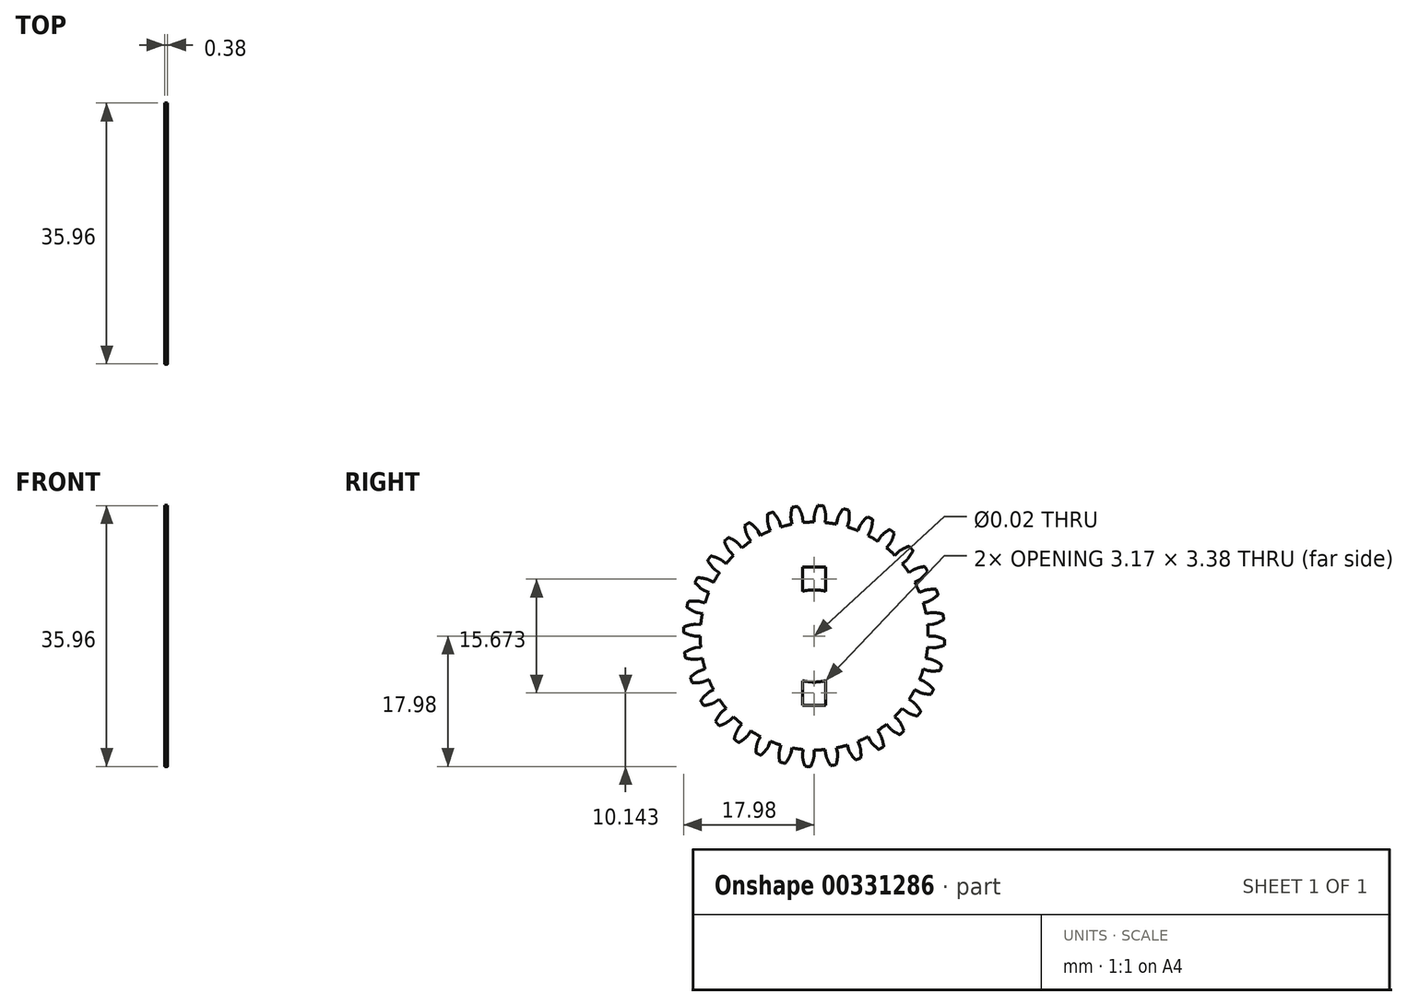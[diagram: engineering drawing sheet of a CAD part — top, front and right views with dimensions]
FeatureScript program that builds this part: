
annotation { "Feature Type Name" : "Feature", "Feature Type Description" : "" }
export const myFeature = defineFeature(function(context is Context, id is Id, definition is map)
    precondition{}
    {
        {
            assignVariable(context, id + "F0", {"name" : "NumberTeeth", "anyValue" : 32});
        }
        {
            assignVariable(context, id + "F1", {"name" : "GearThickness", "anyValue" : 0.38});
        }
        {
            var Q0;
            Q0=qCreatedBy(makeId("Right.planeOp"),FACE);
            var sketch = newSketch(context, id + "F2", { "sketchPlane" : qUnion([Q0])});
            skCircle(sketch, "E0", {"center": v(0, 0) * mm, "radius": 15.7 * mm});
            skCircle(sketch, "E1", {"center": v(0, 0) * mm, "radius": 16.4 * mm, "construction": true});
            skCircle(sketch, "E2", {"center": v(0, 0) * mm, "radius": 16.93 * mm, "construction": true});
            skCircle(sketch, "E3", {"center": v(0, 0) * mm, "radius": 18 * mm});
            skLineSegment(sketch, "E4", {"start": v(0, 0) * mm, "end": v(-16.4, 0) * mm, "construction": true});
            skLineSegment(sketch, "E5.1.0", {"start": v(0, 0) * mm, "end": v(-16.37, 0.82) * mm, "construction": true});
            skLineSegment(sketch, "E5.2.0", {"start": v(0, 0) * mm, "end": v(-16.31, 1.64) * mm, "construction": true});
            skLineSegment(sketch, "E5.3.0", {"start": v(0, 0) * mm, "end": v(-16.2, 2.45) * mm, "construction": true});
            skLineSegment(sketch, "E5.4.0", {"start": v(0, 0) * mm, "end": v(-16.07, 3.26) * mm, "construction": true});
            skLineSegment(sketch, "E5.5.0", {"start": v(0, 0) * mm, "end": v(-15.88, 4.06) * mm, "construction": true});
            skLineSegment(sketch, "E5.6.0", {"start": v(0, 0) * mm, "end": v(-15.66, 4.84) * mm, "construction": true});
            skLineSegment(sketch, "E5.7.0", {"start": v(0, 0) * mm, "end": v(-15.4, 5.62) * mm, "construction": true});
            skLineSegment(sketch, "E5.8.0", {"start": v(0, 0) * mm, "end": v(-15.1, 6.38) * mm, "construction": true});
            skLineSegment(sketch, "E5.9.0", {"start": v(0, 0) * mm, "end": v(-14.76, 7.13) * mm, "construction": true});
            skLineSegment(sketch, "E5.10.0", {"start": v(0, 0) * mm, "end": v(-14.39, 7.86) * mm, "construction": true});
            skLineSegment(sketch, "E5.11.0", {"start": v(0, 0) * mm, "end": v(-13.98, 8.57) * mm, "construction": true});
            skLineSegment(sketch, "E5.12.0", {"start": v(0, 0) * mm, "end": v(-13.53, 9.26) * mm, "construction": true});
            skLineSegment(sketch, "E5.13.0", {"start": v(0, 0) * mm, "end": v(-13.05, 9.92) * mm, "construction": true});
            skLineSegment(sketch, "E5.14.0", {"start": v(0, 0) * mm, "end": v(-12.54, 10.56) * mm, "construction": true});
            skLineSegment(sketch, "E5.anchor2", {"start": v(0, 0) * mm, "end": v(-12.54, 10.56) * mm, "construction": true});
            skLineSegment(sketch, "E6", {"start": v(-16.37, 0.82) * mm, "end": v(-16.41, 0) * mm, "construction": true});
            skLineSegment(sketch, "E7", {"start": v(-16.31, 1.64) * mm, "end": v(-16.48, 0) * mm, "construction": true});
            skLineSegment(sketch, "E8", {"start": v(-16.2, 2.45) * mm, "end": v(-16.58, 0.02) * mm, "construction": true});
            skLineSegment(sketch, "E9", {"start": v(-15.88, 4.06) * mm, "end": v(-16.9, 0.08) * mm, "construction": true});
            skLineSegment(sketch, "E10", {"start": v(-15.66, 4.84) * mm, "end": v(-17.12, 0.15) * mm, "construction": true});
            skLineSegment(sketch, "E11", {"start": v(-15.4, 5.62) * mm, "end": v(-17.37, 0.23) * mm, "construction": true});
            skLineSegment(sketch, "E12", {"start": v(-15.1, 6.38) * mm, "end": v(-17.65, 0.34) * mm, "construction": true});
            skLineSegment(sketch, "E13", {"start": v(-14.76, 7.13) * mm, "end": v(-17.97, 0.49) * mm, "construction": true});
            skLineSegment(sketch, "E14", {"start": v(-14.39, 7.86) * mm, "end": v(-18.32, 0.67) * mm, "construction": true});
            skLineSegment(sketch, "E15", {"start": v(-13.98, 8.57) * mm, "end": v(-18.69, 0.88) * mm, "construction": true});
            skLineSegment(sketch, "E16", {"start": v(-16.07, 3.26) * mm, "end": v(-16.72, 0.04) * mm, "construction": true});
            skLineSegment(sketch, "E17", {"start": v(-13.53, 9.26) * mm, "end": v(-19.08, 1.14) * mm, "construction": true});
            skLineSegment(sketch, "E18", {"start": v(-13.05, 9.92) * mm, "end": v(-19.5, 1.44) * mm, "construction": true});
            skLineSegment(sketch, "E19", {"start": v(-12.54, 10.56) * mm, "end": v(-19.93, 1.78) * mm, "construction": true});
            skLineSegment(sketch, "E20", {"start": v(0, 0) * mm, "end": v(-16.37, 0.8) * mm, "construction": true});
            skLineSegment(sketch, "E21", {"start": v(-15.7, 0) * mm, "end": v(-16.4, 0) * mm});
            skLineSegment(sketch, "E22.MirrorCS", {"start": v(-15.63, 1.54) * mm, "end": v(-16.32, 1.6) * mm});
            skFitSpline(sketch, "E23", {"points": [v(-16.4, 0) * mm, v(-16.41, 0) * mm, v(-16.48, 0) * mm, v(-16.58, 0.02) * mm, v(-16.72, 0.04) * mm, v(-16.9, 0.08) * mm, v(-17.12, 0.15) * mm, v(-17.37, 0.23) * mm, v(-17.65, 0.34) * mm, v(-17.97, 0.49) * mm, v(-18.32, 0.67) * mm, v(-18.69, 0.88) * mm, v(-19.08, 1.14) * mm, v(-19.5, 1.44) * mm, v(-19.93, 1.78) * mm], "startDerivative": vector(-0.8, 0) * mm, "endDerivative": vector(-1.23, 1.03) * mm});
            skLineSegment(sketch, "E24", {"start": v(-19.5, 1.42) * mm, "end": v(-19.93, 1.78) * mm, "construction": true});
            skFitSpline(sketch, "E25.MirrorCS", {"points": [v(-16.32, 1.6) * mm, v(-16.34, 1.6) * mm, v(-16.4, 1.6) * mm, v(-16.5, 1.6) * mm, v(-16.64, 1.6) * mm, v(-16.83, 1.57) * mm, v(-17.05, 1.53) * mm, v(-17.3, 1.47) * mm, v(-17.6, 1.39) * mm, v(-17.93, 1.28) * mm, v(-18.3, 1.13) * mm, v(-18.69, 0.95) * mm, v(-19.1, 0.74) * mm, v(-19.55, 0.48) * mm, v(-20.01, 0.18) * mm], "startDerivative": vector(-0.8, 0.08) * mm, "endDerivative": vector(-1.32, -0.9) * mm});
            skSolve(sketch);
        }
        {
            var Q0;
            {var subQ0=sQuery(id+"F2.wireOp",EDGE,"E0");var subQ27=makeQuery(id+"F2.imprint","INTERSECT",VERTEX,{"derivedFrom":[subQ0,sQuery(id+"F2.wireOp",EDGE,"10ea1024-8cf5-41f5-a75f-a634b86921f3.10.0")]});Q0=makeQuery(id+"F2.imprint","IMPRINT",FACE,{"disambiguationData":[TD([[makeQuery(id+"F2.imprint","IMPRINT",EDGE,{"disambiguationData":[TD([[subQ27,-1.0]])],"derivedFrom":subQ0}),1.0]])]});}
            var Q1;
            {var subQ0=sQuery(id+"F2.wireOp",EDGE,"10ea1024-8cf5-41f5-a75f-a634b86921f3.1.0");Q1=makeQuery(id+"F2.imprint","IMPRINT",FACE,{"disambiguationData":[TD([[makeQuery(id+"F2.imprint","IMPRINT",EDGE,{"derivedFrom":subQ0}),-1.0]])]});}
            var Q2;
            {var subQ7=sQuery(id+"F2.wireOp",EDGE,"10ea1024-8cf5-41f5-a75f-a634b86921f3.2.0");Q2=makeQuery(id+"F2.imprint","IMPRINT",FACE,{"disambiguationData":[TD([[makeQuery(id+"F2.imprint","IMPRINT",EDGE,{"derivedFrom":subQ7}),-1.0]])]});}
            var Q3;
            {var subQ8=sQuery(id+"F2.wireOp",EDGE,"10ea1024-8cf5-41f5-a75f-a634b86921f3.3.0");Q3=makeQuery(id+"F2.imprint","IMPRINT",FACE,{"disambiguationData":[TD([[makeQuery(id+"F2.imprint","IMPRINT",EDGE,{"derivedFrom":subQ8}),-1.0]])]});}
            var Q4;
            {var subQ2=sQuery(id+"F2.wireOp",EDGE,"10ea1024-8cf5-41f5-a75f-a634b86921f3.4.0");Q4=makeQuery(id+"F2.imprint","IMPRINT",FACE,{"disambiguationData":[TD([[makeQuery(id+"F2.imprint","IMPRINT",EDGE,{"derivedFrom":subQ2}),-1.0]])]});}
            var Q5;
            {var subQ8=sQuery(id+"F2.wireOp",EDGE,"10ea1024-8cf5-41f5-a75f-a634b86921f3.5.0");Q5=makeQuery(id+"F2.imprint","IMPRINT",FACE,{"disambiguationData":[TD([[makeQuery(id+"F2.imprint","IMPRINT",EDGE,{"derivedFrom":subQ8}),-1.0]])]});}
            var Q6;
            {var subQ3=sQuery(id+"F2.wireOp",EDGE,"10ea1024-8cf5-41f5-a75f-a634b86921f3.6.0");Q6=makeQuery(id+"F2.imprint","IMPRINT",FACE,{"disambiguationData":[TD([[makeQuery(id+"F2.imprint","IMPRINT",EDGE,{"derivedFrom":subQ3}),-1.0]])]});}
            var Q7;
            {var subQ0=sQuery(id+"F2.wireOp",EDGE,"10ea1024-8cf5-41f5-a75f-a634b86921f3.7.0");Q7=makeQuery(id+"F2.imprint","IMPRINT",FACE,{"disambiguationData":[TD([[makeQuery(id+"F2.imprint","IMPRINT",EDGE,{"derivedFrom":subQ0}),-1.0]])]});}
            var Q8;
            {var subQ5=sQuery(id+"F2.wireOp",EDGE,"10ea1024-8cf5-41f5-a75f-a634b86921f3.8.0");Q8=makeQuery(id+"F2.imprint","IMPRINT",FACE,{"disambiguationData":[TD([[makeQuery(id+"F2.imprint","IMPRINT",EDGE,{"derivedFrom":subQ5}),-1.0]])]});}
            var Q9;
            {var subQ1=sQuery(id+"F2.wireOp",EDGE,"10ea1024-8cf5-41f5-a75f-a634b86921f3.9.0");Q9=makeQuery(id+"F2.imprint","IMPRINT",FACE,{"disambiguationData":[TD([[makeQuery(id+"F2.imprint","IMPRINT",EDGE,{"derivedFrom":subQ1}),-1.0]])]});}
            var Q10;
            {var subQ5=sQuery(id+"F2.wireOp",EDGE,"10ea1024-8cf5-41f5-a75f-a634b86921f3.10.0");Q10=makeQuery(id+"F2.imprint","IMPRINT",FACE,{"disambiguationData":[TD([[makeQuery(id+"F2.imprint","IMPRINT",EDGE,{"derivedFrom":subQ5}),-1.0]])]});}
            var Q11;
            {var subQ8=sQuery(id+"F2.wireOp",EDGE,"10ea1024-8cf5-41f5-a75f-a634b86921f3.11.0");Q11=makeQuery(id+"F2.imprint","IMPRINT",FACE,{"disambiguationData":[TD([[makeQuery(id+"F2.imprint","IMPRINT",EDGE,{"derivedFrom":subQ8}),-1.0]])]});}
            var Q12;
            {var subQ2=sQuery(id+"F2.wireOp",EDGE,"10ea1024-8cf5-41f5-a75f-a634b86921f3.12.0");Q12=makeQuery(id+"F2.imprint","IMPRINT",FACE,{"disambiguationData":[TD([[makeQuery(id+"F2.imprint","IMPRINT",EDGE,{"derivedFrom":subQ2}),-1.0]])]});}
            var Q13;
            {var subQ3=sQuery(id+"F2.wireOp",EDGE,"10ea1024-8cf5-41f5-a75f-a634b86921f3.13.0");Q13=makeQuery(id+"F2.imprint","IMPRINT",FACE,{"disambiguationData":[TD([[makeQuery(id+"F2.imprint","IMPRINT",EDGE,{"derivedFrom":subQ3}),-1.0]])]});}
            var Q14;
            {var subQ0=sQuery(id+"F2.wireOp",EDGE,"10ea1024-8cf5-41f5-a75f-a634b86921f3.14.0");Q14=makeQuery(id+"F2.imprint","IMPRINT",FACE,{"disambiguationData":[TD([[makeQuery(id+"F2.imprint","IMPRINT",EDGE,{"derivedFrom":subQ0}),-1.0]])]});}
            var Q15;
            {var subQ6=sQuery(id+"F2.wireOp",EDGE,"10ea1024-8cf5-41f5-a75f-a634b86921f3.15.0");Q15=makeQuery(id+"F2.imprint","IMPRINT",FACE,{"disambiguationData":[TD([[makeQuery(id+"F2.imprint","IMPRINT",EDGE,{"derivedFrom":subQ6}),-1.0]])]});}
            var Q16;
            {var subQ5=sQuery(id+"F2.wireOp",EDGE,"10ea1024-8cf5-41f5-a75f-a634b86921f3.16.0");Q16=makeQuery(id+"F2.imprint","IMPRINT",FACE,{"disambiguationData":[TD([[makeQuery(id+"F2.imprint","IMPRINT",EDGE,{"derivedFrom":subQ5}),-1.0]])]});}
            var Q17;
            {var subQ7=sQuery(id+"F2.wireOp",EDGE,"10ea1024-8cf5-41f5-a75f-a634b86921f3.17.0");Q17=makeQuery(id+"F2.imprint","IMPRINT",FACE,{"disambiguationData":[TD([[makeQuery(id+"F2.imprint","IMPRINT",EDGE,{"derivedFrom":subQ7}),-1.0]])]});}
            var Q18;
            {var subQ5=sQuery(id+"F2.wireOp",EDGE,"10ea1024-8cf5-41f5-a75f-a634b86921f3.18.0");Q18=makeQuery(id+"F2.imprint","IMPRINT",FACE,{"disambiguationData":[TD([[makeQuery(id+"F2.imprint","IMPRINT",EDGE,{"derivedFrom":subQ5}),-1.0]])]});}
            var Q19;
            {var subQ8=sQuery(id+"F2.wireOp",EDGE,"10ea1024-8cf5-41f5-a75f-a634b86921f3.19.0");Q19=makeQuery(id+"F2.imprint","IMPRINT",FACE,{"disambiguationData":[TD([[makeQuery(id+"F2.imprint","IMPRINT",EDGE,{"derivedFrom":subQ8}),-1.0]])]});}
            var Q20;
            {var subQ8=sQuery(id+"F2.wireOp",EDGE,"E21");Q20=makeQuery(id+"F2.imprint","IMPRINT",FACE,{"disambiguationData":[TD([[makeQuery(id+"F2.imprint","IMPRINT",EDGE,{"derivedFrom":subQ8}),-1.0]])]});}
            extrude(context, id + "F3", {"entities" : qUnion([Q0, Q1, Q2, Q3, Q4, Q5, Q6, Q7, Q8, Q9, Q10, Q11, Q12, Q13, Q14, Q15, Q16, Q17, Q18, Q19, Q20]), "depth" : (getVariable(context, 'GearThickness')) * mm});
        }
        {
            var Q0;
            Q0=makeQuery(id+"F3.opExtrude","SWEPT_FACE",FACE,{"disambiguationData":[OSD([sQuery(id+"F2.wireOp",EDGE,"E25.MirrorCS")])]});
            var Q1;
            Q1=makeQuery(id+"F3.opExtrude","SWEPT_FACE",FACE,{"disambiguationData":[OSD([sQuery(id+"F2.wireOp",EDGE,"E23")])]});
            var Q2;
            Q2=makeQuery(id+"F3.opExtrude","SWEPT_FACE",FACE,{"disambiguationData":[OSD([sQuery(id+"F2.wireOp",EDGE,"E3")])]});
            var Q3;
            Q3=makeQuery(id+"F3.opExtrude","SWEPT_FACE",FACE,{"disambiguationData":[OSD([sQuery(id+"F2.wireOp",EDGE,"E22.MirrorCS")])]});
            var Q4;
            Q4=makeQuery(id+"F3.opExtrude","SWEPT_FACE",FACE,{"disambiguationData":[OSD([sQuery(id+"F2.wireOp",EDGE,"E21")])]});
            var Q5;
            Q5=makeQuery(id+"F3.opExtrude","SWEPT_FACE",FACE,{"disambiguationData":[OSD([sQuery(id+"F2.wireOp",EDGE,"E0")])]});
            circularPattern(context, id + "F4", {"faces" : qUnion([Q0, Q1, Q2, Q3, Q4]), "axis" : qUnion([Q5]), "angle" : 360 * degree, "instanceCount" : getVariable(context, 'NumberTeeth'), "equalSpace" : true, "patternType" : PatternType.FACE});
        }
        {
            var Q0;
            Q0=sQuery(id+"F2.wireOp",VERTEX,"E0.center");
            var Q1;
            Q1=makeQuery(id+"F3.opExtrude","SWEPT_BODY",BODY,{"disambiguationData":[OSD([sQuery(id+"F2.wireOp",EDGE,"E0"),sQuery(id+"F2.wireOp",EDGE,"E3"),sQuery(id+"F2.wireOp",EDGE,"E21"),sQuery(id+"F2.wireOp",EDGE,"E22.MirrorCS"),sQuery(id+"F2.wireOp",EDGE,"E23"),sQuery(id+"F2.wireOp",EDGE,"E25.MirrorCS")])]});
            hole(context, id + "F5", {"style" : HoleStyle.SIMPLE, "endStyle" : HoleEndStyle.THROUGH, "oppositeDirection" : true, "standardTappedOrClearance" : lookupTablePath({ "standard" : "ANSI", "size" : "1/2 (0.5)", "type" : "Drilled" }), "standardBlindInLast" : lookupTablePath({ "standard" : "ANSI", "size" : "1/2", "type" : "Drilled" }), "holeDiameter" : 1 / 50.8 * mm, "tappedDepth" : 12.7 * mm, "tapClearance" : 3, "locations" : qUnion([Q0]), "scope" : qUnion([Q1])});
        }
        {
            var Q0;
            Q0=makeQuery(id+"F3.opExtrude","CAP_FACE",FACE,{"disambiguationData":[OSD([sQuery(id+"F2.wireOp",EDGE,"E0"),sQuery(id+"F2.wireOp",EDGE,"E3"),sQuery(id+"F2.wireOp",EDGE,"E21"),sQuery(id+"F2.wireOp",EDGE,"E22.MirrorCS"),sQuery(id+"F2.wireOp",EDGE,"E23"),sQuery(id+"F2.wireOp",EDGE,"E25.MirrorCS")])],"isStart":true});
            var sketch = newSketch(context, id + "F6", { "sketchPlane" : qUnion([Q0])});
            skCircle(sketch, "E26.0", {"center": v(0, 0) * mm, "radius": 6.35 * mm});
            skLineSegment(sketch, "E27.bottom", {"start": v(1.59, -9.53) * mm, "end": v(-1.59, -9.53) * mm});
            skLineSegment(sketch, "E27.top", {"start": v(1.59, 9.53) * mm, "end": v(-1.59, 9.53) * mm});
            skLineSegment(sketch, "E27.left", {"start": v(1.59, -9.53) * mm, "end": v(1.59, 9.53) * mm});
            skLineSegment(sketch, "E27.right", {"start": v(-1.59, -9.53) * mm, "end": v(-1.59, 9.53) * mm});
            skSolve(sketch);
        }
        {
            var Q0;
            {var subQ5=sQuery(id+"F6.wireOp",EDGE,"E27.bottom");Q0=makeQuery(id+"F6.imprint","IMPRINT",FACE,{"disambiguationData":[TD([[makeQuery(id+"F6.imprint","IMPRINT",EDGE,{"derivedFrom":subQ5}),-1.0]])]});}
            var Q1;
            {var subQ5=sQuery(id+"F6.wireOp",EDGE,"E27.top");Q1=makeQuery(id+"F6.imprint","IMPRINT",FACE,{"disambiguationData":[TD([[makeQuery(id+"F6.imprint","IMPRINT",EDGE,{"derivedFrom":subQ5}),1.0]])]});}
            extrude(context, id + "F7", {"entities" : qUnion([Q0, Q1]), "operationType" : NewBodyOperationType.REMOVE, "endBound" : BoundingType.UP_TO_NEXT, "oppositeDirection" : true, "depth" : 25.4 * mm});
        }
    });
